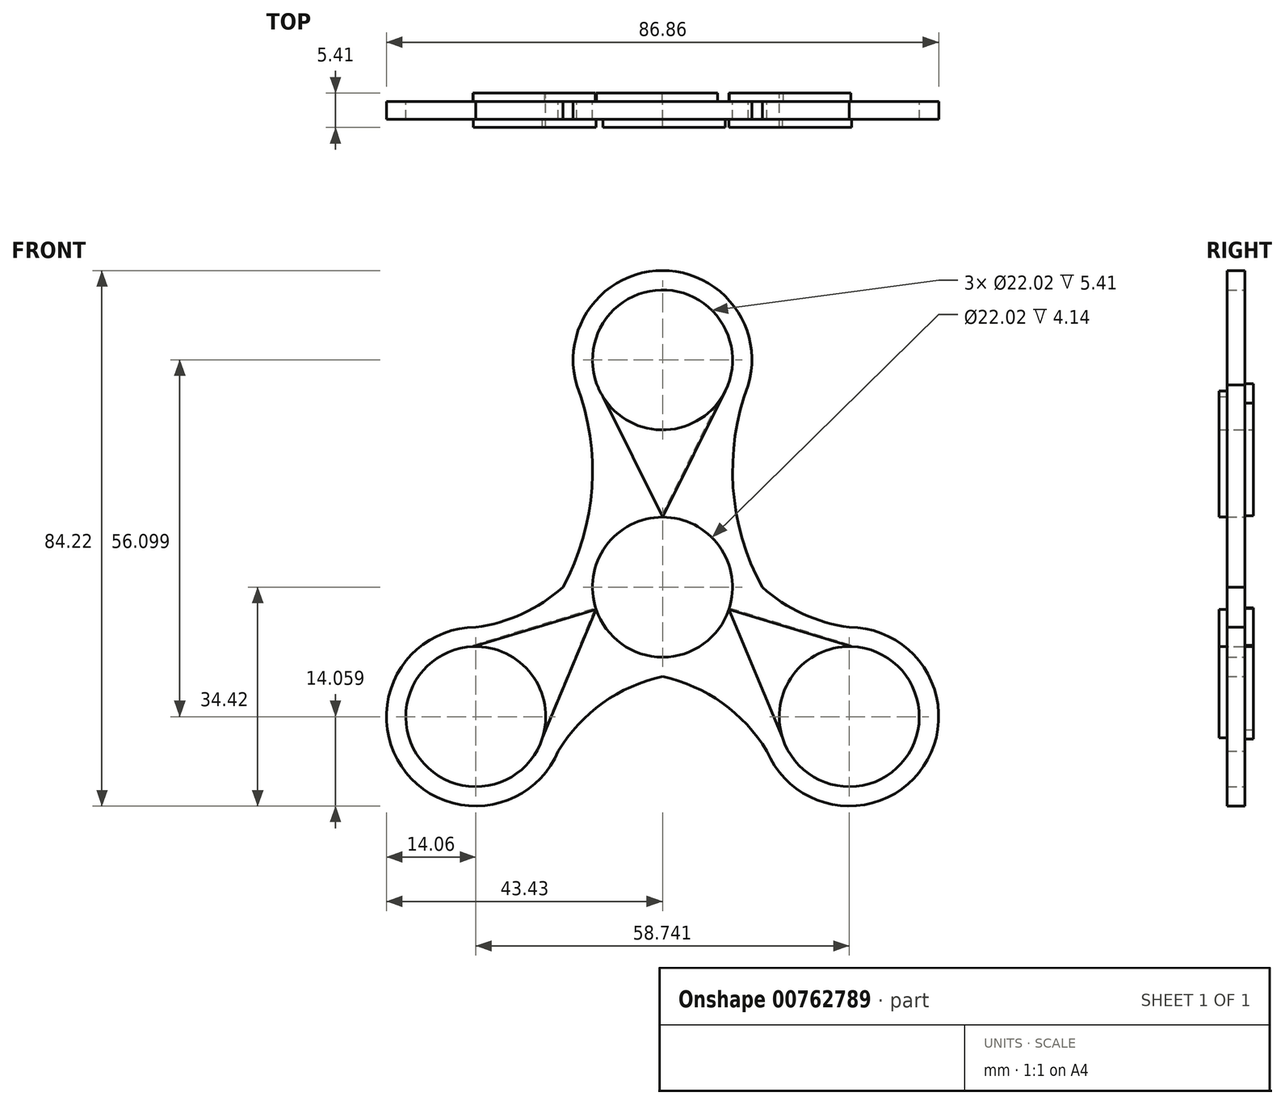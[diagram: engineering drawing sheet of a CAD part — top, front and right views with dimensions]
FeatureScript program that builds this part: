
annotation { "Feature Type Name" : "Feature", "Feature Type Description" : "" }
export const myFeature = defineFeature(function(context is Context, id is Id, definition is map)
    precondition{}
    {
        {
            var Q0;
            Q0=qCreatedBy(makeId("Front.planeOp"),FACE);
            var sketch = newSketch(context, id + "F0", { "sketchPlane" : qUnion([Q0])});
            skCircle(sketch, "E0", {"center": v(0, 0) * mm, "radius": 11.01 * mm});
            skCircle(sketch, "E1", {"center": v(-29.37, -20.36) * mm, "radius": 11.01 * mm});
            skCircle(sketch, "E2", {"center": v(29.37, -20.36) * mm, "radius": 11.01 * mm});
            skCircle(sketch, "E3", {"center": v(0, 35.74) * mm, "radius": 11.01 * mm});
            skCircle(sketch, "E4", {"center": v(0, 35.74) * mm, "radius": 14.06 * mm});
            skCircle(sketch, "E5", {"center": v(-29.37, -20.36) * mm, "radius": 14.06 * mm});
            skCircle(sketch, "E6", {"center": v(29.37, -20.36) * mm, "radius": 14.06 * mm});
            skCircle(sketch, "E7", {"center": v(0, 0) * mm, "radius": 14.06 * mm});
            skArc(sketch, "E8", {"start": v(0, -14.06) * mm, "mid": v(-9.4, -18.22) * mm, "end": v(-16.4, -25.77) * mm});
            skArc(sketch, "E9", {"start": v(16.4, -25.77) * mm, "mid": v(9.4, -18.22) * mm, "end": v(0, -14.06) * mm});
            skArc(sketch, "E10", {"start": v(-29.37, -6.3) * mm, "mid": v(-22.05, -4.19) * mm, "end": v(-15.68, 0) * mm});
            skArc(sketch, "E11", {"start": v(-15.68, 0) * mm, "mid": v(-11.1, 15.66) * mm, "end": v(-13.5, 31.8) * mm});
            skArc(sketch, "E12", {"start": v(15.69, 0) * mm, "mid": v(22.05, -4.19) * mm, "end": v(29.37, -6.3) * mm});
            skArc(sketch, "E13", {"start": v(13.5, 31.8) * mm, "mid": v(11.1, 15.66) * mm, "end": v(15.69, 0) * mm});
            skSolve(sketch);
        }
        {
            var Q0;
            Q0=makeQuery(id+"F0.imprint","IMPRINT",FACE,{"disambiguationData":[TD([[makeQuery(id+"F0.imprint","IMPRINT",EDGE,{"derivedFrom":sQuery(id+"F0.wireOp",EDGE,"E2")}),-1.0]])]});
            var Q1;
            Q1=makeQuery(id+"F0.imprint","IMPRINT",FACE,{"disambiguationData":[TD([[makeQuery(id+"F0.imprint","IMPRINT",EDGE,{"derivedFrom":sQuery(id+"F0.wireOp",EDGE,"E7")}),-1.0]])]});
            var Q2;
            Q2=makeQuery(id+"F0.imprint","IMPRINT",FACE,{"disambiguationData":[TD([[makeQuery(id+"F0.imprint","IMPRINT",EDGE,{"derivedFrom":sQuery(id+"F0.wireOp",EDGE,"E0")}),-1.0]])]});
            var Q3;
            Q3=makeQuery(id+"F0.imprint","IMPRINT",FACE,{"disambiguationData":[TD([[makeQuery(id+"F0.imprint","IMPRINT",EDGE,{"derivedFrom":sQuery(id+"F0.wireOp",EDGE,"E1")}),-1.0]])]});
            var Q4;
            Q4=makeQuery(id+"F0.imprint","IMPRINT",FACE,{"disambiguationData":[TD([[makeQuery(id+"F0.imprint","IMPRINT",EDGE,{"derivedFrom":sQuery(id+"F0.wireOp",EDGE,"E3")}),-1.0]])]});
            extrude(context, id + "F1", {"entities" : qUnion([Q0, Q1, Q2, Q3, Q4]), "depth" : 2.8 * mm, "offsetDistance" : 25.4 * mm});
        }
        {
            var Q0;
            Q0=makeQuery(id+"F1.opExtrude","CAP_FACE",FACE,{"disambiguationData":[OSD([sQuery(id+"F0.wireOp",EDGE,"E0"),sQuery(id+"F0.wireOp",EDGE,"E1"),sQuery(id+"F0.wireOp",EDGE,"E2"),sQuery(id+"F0.wireOp",EDGE,"E3"),sQuery(id+"F0.wireOp",EDGE,"E4"),sQuery(id+"F0.wireOp",EDGE,"E5"),sQuery(id+"F0.wireOp",EDGE,"E6"),sQuery(id+"F0.wireOp",EDGE,"E8"),sQuery(id+"F0.wireOp",EDGE,"E9"),sQuery(id+"F0.wireOp",EDGE,"BPdNb8MT-WSfi-Rhgm-Mg9X-nEWEoWId4Fqx"),sQuery(id+"F0.wireOp",EDGE,"EkAl8I3m-FOp9-Qzrx-Iycw-aUJjQnWCx5jD"),sQuery(id+"F0.wireOp",EDGE,"631e6540-c3dc-4946-9f20-392bf4cbb8ff0.MirrorCS"),sQuery(id+"F0.wireOp",EDGE,"4e9ab6db-9015-4a45-b927-c8f4f14878bc0.MirrorCS"),sQuery(id+"F0.wireOp",EDGE,"CivjGbcd-qVmX-ZDLO-T6yC-1PznIG7T6Q2j")])],"isStart":false});
            var sketch = newSketch(context, id + "F2", { "sketchPlane" : qUnion([Q0])});
            skLineSegment(sketch, "E14", {"start": v(0, 11.01) * mm, "end": v(-10.28, 31.8) * mm});
            skLineSegment(sketch, "E15", {"start": v(0, 11.01) * mm, "end": v(10.34, 31.8) * mm});
            skLineSegment(sketch, "E16", {"start": v(-10.28, 31.8) * mm, "end": v(10.34, 31.8) * mm});
            skLineSegment(sketch, "E17", {"start": v(29.75, -9.36) * mm, "end": v(10.45, -3.48) * mm});
            skLineSegment(sketch, "E18", {"start": v(10.45, -3.48) * mm, "end": v(19.62, -25.48) * mm});
            skLineSegment(sketch, "E19", {"start": v(-29.75, -9.36) * mm, "end": v(-10.45, -3.48) * mm});
            skLineSegment(sketch, "E20", {"start": v(-19.62, -25.48) * mm, "end": v(-10.45, -3.48) * mm});
            skSolve(sketch);
        }
        {
            var Q0;
            {var subQ0=sQuery(id+"F2.wireOp",EDGE,"E19");Q0=makeQuery(id+"F2.imprint","IMPRINT",FACE,{"disambiguationData":[TD([[makeQuery(id+"F2.imprint","IMPRINT",EDGE,{"derivedFrom":subQ0}),-1.0]])]});}
            var Q1;
            {var subQ0=sQuery(id+"F2.wireOp",EDGE,"E17");Q1=makeQuery(id+"F2.imprint","IMPRINT",FACE,{"disambiguationData":[TD([[makeQuery(id+"F2.imprint","IMPRINT",EDGE,{"derivedFrom":subQ0}),1.0]])]});}
            var Q2;
            {var subQ1=sQuery(id+"F2.wireOp",EDGE,"E14");var subQ3=makeQuery(id+"F1.opExtrude","CAP_EDGE",EDGE,{"disambiguationData":[OSD([sQuery(id+"F0.wireOp",EDGE,"E3")])],"isStart":false});var subQ4=makeQuery(id+"F2.imprint","INTERSECT",VERTEX,{"derivedFrom":[subQ3,subQ1]});Q2=makeQuery(id+"F2.imprint","IMPRINT",FACE,{"disambiguationData":[TD([[makeQuery(id+"F2.imprint","IMPRINT",EDGE,{"disambiguationData":[TD([[subQ4,-1.0]])],"derivedFrom":subQ3}),-1.0]])]});}
            extrude(context, id + "F3", {"entities" : qUnion([Q0, Q1, Q2]), "operationType" : NewBodyOperationType.ADD, "depth" : 1.27 * mm, "offsetDistance" : 25.4 * mm});
        }
        {
            var Q0;
            Q0=makeQuery(id+"F1.opExtrude","CAP_FACE",FACE,{"disambiguationData":[OSD([sQuery(id+"F0.wireOp",EDGE,"E0"),sQuery(id+"F0.wireOp",EDGE,"E1"),sQuery(id+"F0.wireOp",EDGE,"E2"),sQuery(id+"F0.wireOp",EDGE,"E3"),sQuery(id+"F0.wireOp",EDGE,"E4"),sQuery(id+"F0.wireOp",EDGE,"E5"),sQuery(id+"F0.wireOp",EDGE,"E6"),sQuery(id+"F0.wireOp",EDGE,"E8"),sQuery(id+"F0.wireOp",EDGE,"E9"),sQuery(id+"F0.wireOp",EDGE,"BPdNb8MT-WSfi-Rhgm-Mg9X-nEWEoWId4Fqx"),sQuery(id+"F0.wireOp",EDGE,"EkAl8I3m-FOp9-Qzrx-Iycw-aUJjQnWCx5jD"),sQuery(id+"F0.wireOp",EDGE,"631e6540-c3dc-4946-9f20-392bf4cbb8ff0.MirrorCS"),sQuery(id+"F0.wireOp",EDGE,"4e9ab6db-9015-4a45-b927-c8f4f14878bc0.MirrorCS"),sQuery(id+"F0.wireOp",EDGE,"CivjGbcd-qVmX-ZDLO-T6yC-1PznIG7T6Q2j")])],"isStart":true});
            var sketch = newSketch(context, id + "F4", { "sketchPlane" : qUnion([Q0])});
            skLineSegment(sketch, "E21", {"start": v(0.1, 11.22) * mm, "end": v(-10.18, 32) * mm});
            skLineSegment(sketch, "E22", {"start": v(0.1, 11.22) * mm, "end": v(10.44, 32) * mm});
            skLineSegment(sketch, "E23", {"start": v(-10.18, 32) * mm, "end": v(10.44, 32) * mm});
            skLineSegment(sketch, "E24", {"start": v(29.85, -9.15) * mm, "end": v(10.55, -3.27) * mm});
            skLineSegment(sketch, "E25", {"start": v(10.55, -3.27) * mm, "end": v(19.72, -25.27) * mm});
            skLineSegment(sketch, "E26", {"start": v(-29.64, -9.15) * mm, "end": v(-10.34, -3.27) * mm});
            skLineSegment(sketch, "E27", {"start": v(-19.51, -25.27) * mm, "end": v(-10.34, -3.27) * mm});
            skLineSegment(sketch, "E28", {"start": v(-29.64, -9.15) * mm, "end": v(-19.51, -25.27) * mm});
            skLineSegment(sketch, "E29", {"start": v(19.72, -25.27) * mm, "end": v(29.85, -9.15) * mm});
            skSolve(sketch);
        }
        {
            var Q0;
            {var subQ0=sQuery(id+"F4.wireOp",EDGE,"E22");Q0=makeQuery(id+"F4.imprint","IMPRINT",FACE,{"disambiguationData":[TD([[makeQuery(id+"F4.imprint","IMPRINT",EDGE,{"derivedFrom":subQ0}),1.0]])]});}
            var Q1;
            {var subQ0=sQuery(id+"F4.wireOp",EDGE,"E24");Q1=makeQuery(id+"F4.imprint","IMPRINT",FACE,{"disambiguationData":[TD([[makeQuery(id+"F4.imprint","IMPRINT",EDGE,{"derivedFrom":subQ0}),1.0]])]});}
            var Q2;
            {var subQ3=sQuery(id+"F4.wireOp",EDGE,"E28");var subQ7=sQuery(id+"F4.wireOp",EDGE,"E26");var subQ8=makeQuery(id+"F4.imprint","INTERSECT",VERTEX,{"derivedFrom":[subQ7,subQ3]});Q2=makeQuery(id+"F4.imprint","IMPRINT",FACE,{"disambiguationData":[TD([[makeQuery(id+"F4.imprint","IMPRINT",EDGE,{"disambiguationData":[TD([[subQ8,-1.0]])],"derivedFrom":subQ7}),-1.0]])]});}
            extrude(context, id + "F5", {"entities" : qUnion([Q0, Q1, Q2]), "operationType" : NewBodyOperationType.ADD, "depth" : 1.35 * mm, "offsetDistance" : 25.4 * mm});
        }
    });
